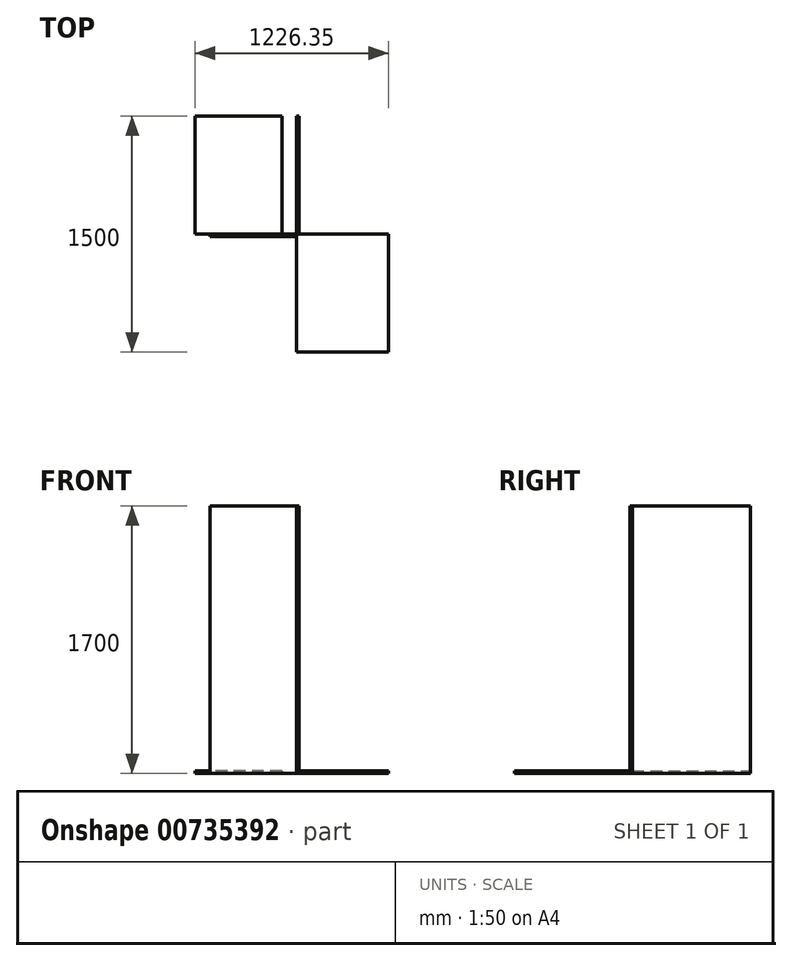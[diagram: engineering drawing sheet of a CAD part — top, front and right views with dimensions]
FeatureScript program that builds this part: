
annotation { "Feature Type Name" : "Feature", "Feature Type Description" : "" }
export const myFeature = defineFeature(function(context is Context, id is Id, definition is map)
    precondition{}
    {
        {
            var Q0;
            Q0=qCreatedBy(makeId("Right.planeOp"),FACE);
            var sketch = newSketch(context, id + "F0", { "sketchPlane" : qUnion([Q0])});
            skLineSegment(sketch, "E0.bottom", {"start": v(0, 0) * mm, "end": v(750, 0) * mm});
            skLineSegment(sketch, "E0.top", {"start": v(0, 1700) * mm, "end": v(750, 1700) * mm});
            skLineSegment(sketch, "E0.left", {"start": v(0, 0) * mm, "end": v(0, 1700) * mm});
            skLineSegment(sketch, "E0.right", {"start": v(750, 0) * mm, "end": v(750, 1700) * mm});
            skSolve(sketch);
        }
        {
            var Q0;
            Q0=makeQuery(id+"F0.imprint","IMPRINT",FACE,{"disambiguationData":[TD([[makeQuery(id+"F0.imprint","IMPRINT",EDGE,{"derivedFrom":sQuery(id+"F0.wireOp",EDGE,"E0.bottom")}),1.0]])]});
            extrude(context, id + "F1", {"entities" : qUnion([Q0]), "depth" : 16 * mm, "offsetDistance" : 25 * mm});
        }
        {
            var Q0;
            Q0=qCreatedBy(makeId("Top.planeOp"),FACE);
            var sketch = newSketch(context, id + "F2", { "sketchPlane" : qUnion([Q0])});
            skLineSegment(sketch, "E1.bottom", {"start": v(-94.35, 0) * mm, "end": v(-644.35, 0) * mm});
            skLineSegment(sketch, "E1.top", {"start": v(-94.35, 750) * mm, "end": v(-644.35, 750) * mm});
            skLineSegment(sketch, "E1.left", {"start": v(-94.35, 0) * mm, "end": v(-94.35, 750) * mm});
            skLineSegment(sketch, "E1.right", {"start": v(-644.35, 0) * mm, "end": v(-644.35, 750) * mm});
            skSolve(sketch);
        }
        {
            var Q0;
            Q0 = qSketchRegion(id + "F2", true);
            extrude(context, id + "F3", {"entities" : qUnion([Q0]), "depth" : 16 * mm, "offsetDistance" : 25 * mm});
        }
        {
            var Q0;
            Q0=qCreatedBy(makeId("Top.planeOp"),FACE);
            var sketch = newSketch(context, id + "F4", { "sketchPlane" : qUnion([Q0])});
            skLineSegment(sketch, "E2.bottom", {"start": v(0, 0) * mm, "end": v(-550, 0) * mm});
            skLineSegment(sketch, "E2.top", {"start": v(0, -16) * mm, "end": v(-550, -16) * mm});
            skLineSegment(sketch, "E2.left", {"start": v(0, 0) * mm, "end": v(0, -16) * mm});
            skLineSegment(sketch, "E2.right", {"start": v(-550, 0) * mm, "end": v(-550, -16) * mm});
            skSolve(sketch);
        }
        {
            var Q0;
            Q0 = qSketchRegion(id + "F4", true);
            extrude(context, id + "F5", {"entities" : qUnion([Q0]), "depth" : 1700 * mm, "offsetDistance" : 25 * mm});
        }
        {
            var Q0;
            Q0=qCreatedBy(makeId("Top.planeOp"),FACE);
            var sketch = newSketch(context, id + "F6", { "sketchPlane" : qUnion([Q0])});
            skLineSegment(sketch, "E3.bottom", {"start": v(0, 0) * mm, "end": v(582, 0) * mm});
            skLineSegment(sketch, "E3.top", {"start": v(0, -750) * mm, "end": v(582, -750) * mm});
            skLineSegment(sketch, "E3.left", {"start": v(0, 0) * mm, "end": v(0, -750) * mm});
            skLineSegment(sketch, "E3.right", {"start": v(582, 0) * mm, "end": v(582, -750) * mm});
            skSolve(sketch);
        }
        {
            var Q0;
            Q0 = qSketchRegion(id + "F6", true);
            extrude(context, id + "F7", {"entities" : qUnion([Q0]), "depth" : 16 * mm, "offsetDistance" : 25 * mm});
        }
    });
